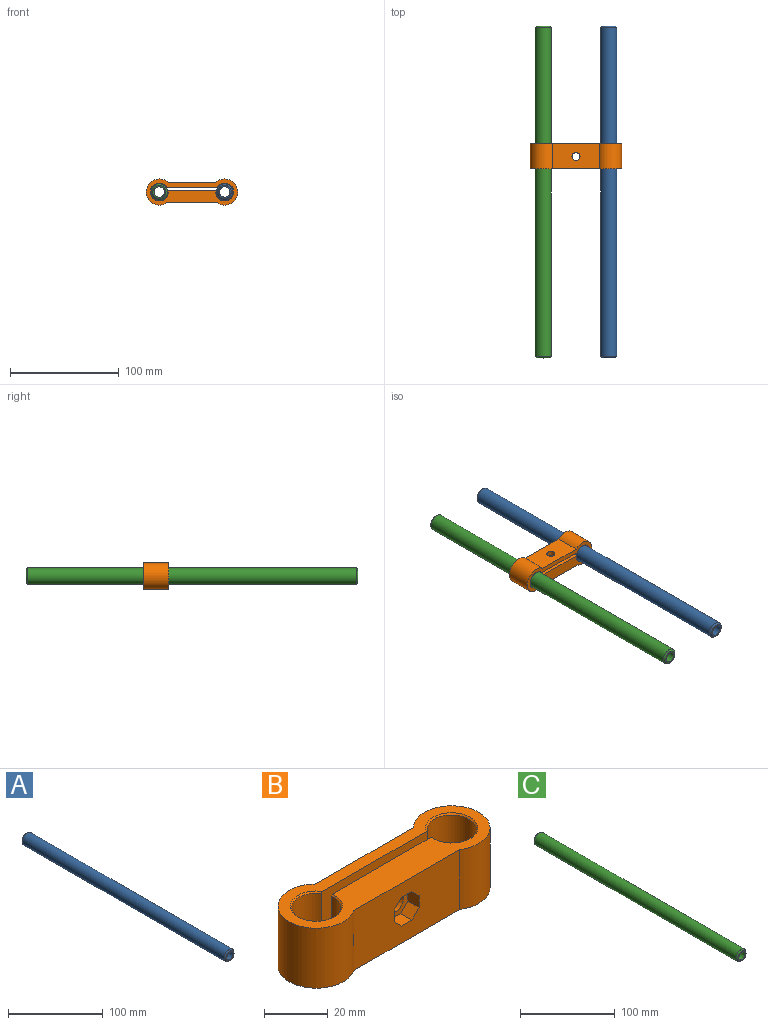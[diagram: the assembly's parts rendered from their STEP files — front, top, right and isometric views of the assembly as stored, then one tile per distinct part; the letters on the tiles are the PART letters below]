
ASSEMBLY  parts=3 mates=3
PART A: 6 faces, bbox 15x304.8x15 mm
  f0: cylinder r=4.8mm len=304.8mm, axis (0,1,0), area 9192.6mm2, adj f2,f3
  f1: cylinder r=7.5mm len=301.8mm, axis (0,1,0), area 14222mm2, adj f4,f5
  f2: plane 12x12mm, normal (0,-1,0), area 40.7mm2, adj f0,f5
  f3: plane 12x12mm, normal (0,1,0), area 40.7mm2, adj f0,f4
  f4: cone r=7.5mm half-angle=45deg, axis (0,-1,0), area 90mm2, adj f1,f3
  f5: cone r=6mm half-angle=45deg, axis (0,1,0), area 90mm2, adj f1,f2
PART B: 25 faces, bbox 84x24x23 mm
  f0: plane 46.87x23mm, normal (0,-1,0), area 977.8mm2, adj f1,f3,f8,f9,f16,f17,f18,f19
  f1: cylinder r=12mm len=24mm, axis (0,0,1), area 1238.6mm2, adj f0,f2,f8,f9
  f2: plane 43.34x23mm, normal (0,1,0), area 954.5mm2, adj f1,f3,f8,f9,f11
  f3: cylinder r=12mm len=24mm, axis (0,0,1), area 1238.6mm2, adj f0,f2,f8,f9
  f4: plane 44.73x23mm, normal (0,1,0), area 985.9mm2, adj f5,f7,f8,f9,f10,f12,f13,f14
  f5: cylinder r=7.7mm len=22mm, axis (0,0,1), area 987.2mm2, adj f4,f6,f12,f15
  f6: plane 47.18x23.01mm, normal (0,-1,0), area 1041.9mm2, adj f5,f7,f8,f9,f11,f12,f13,f14
  f7: cylinder r=7.7mm len=22mm, axis (0,0,1), area 987.2mm2, adj f4,f6,f13,f14
  f8: plane 84x24mm, normal (0,0,-1), area 1061.5mm2, adj f0,f1,f2,f3,f4,f6,f12,f13
  f9: plane 84x24mm, normal (0,0,1), area 1061.5mm2, adj f0,f1,f2,f3,f4,f6,f14,f15
  f10: cylinder r=3.67mm len=7.35mm, axis (0,1,0), area 139.6mm2, adj f4,f24
  f11: cylinder r=3.67mm len=7.35mm, axis (0,1,0), area 101.1mm2, adj f2,f6
  f12: cone r=8.2mm half-angle=45deg, axis (0,0,-1), area 32.9mm2, adj f4,f5,f6,f8
  f13: cone r=7.7mm half-angle=45deg, axis (0,0,-1), area 32.9mm2, adj f4,f6,f7,f8
  f14: cone r=8.2mm half-angle=45deg, axis (0,0,1), area 32.9mm2, adj f4,f6,f7,f9
  f15: cone r=7.7mm half-angle=45deg, axis (0,0,1), area 32.9mm2, adj f4,f5,f6,f9
  f16: plane 5x3.22mm, normal (0.71,0,-0.71), area 22.8mm2, adj f0,f17,f23,f24
  f17: plane 5x4.56mm, normal (1,0,0), area 22.8mm2, adj f0,f16,f18,f24
  f18: plane 5x3.22mm, normal (0.71,0,0.71), area 22.8mm2, adj f0,f17,f19,f24
  f19: plane 5x4.56mm, normal (0,0,1), area 22.8mm2, adj f0,f18,f20,f24
  f20: plane 5x3.22mm, normal (-0.71,0,0.71), area 22.8mm2, adj f0,f19,f21,f24
  f21: plane 5x4.56mm, normal (-1,0,0), area 22.8mm2, adj f0,f20,f22,f24
  f22: plane 5x3.22mm, normal (-0.71,0,-0.71), area 22.8mm2, adj f0,f21,f23,f24
  f23: plane 5x4.56mm, normal (0,0,-1), area 22.8mm2, adj f0,f16,f22,f24
  f24: plane 11x11mm, normal (0,-1,0), area 57.8mm2, adj f10,f16,f17,f18,f19,f20,f21,f22
PART C: 6 faces, bbox 15x304.8x15 mm
  f0: cylinder r=4.8mm len=304.8mm, axis (0,1,0), area 9192.6mm2, adj f2,f3
  f1: cylinder r=7.5mm len=301.8mm, axis (0,1,0), area 14222mm2, adj f4,f5
  f2: plane 12x12mm, normal (0,-1,0), area 40.7mm2, adj f0,f5
  f3: plane 12x12mm, normal (0,1,0), area 40.7mm2, adj f0,f4
  f4: cone r=7.5mm half-angle=45deg, axis (0,-1,0), area 90mm2, adj f1,f3
  f5: cone r=6mm half-angle=45deg, axis (0,1,0), area 90mm2, adj f1,f2
PLACE A rot(axis=(1,0,0),180deg) t=(-45.59,-31.65,-0.84)mm
PLACE B rot(axis=(1,0,0),90deg) t=(-45.64,47.76,-5.84)mm
PLACE C t=(-45.69,-31.65,-0.84)mm
MATE parallel C.f1 <-> A.f1  axis (0,-1,0) through (-75.64,-184.05,-0.84)mm
MATE slider B.f3 <-> C.f1  axis (0,-1,0) through (-75.64,-9.65,-0.84)mm
MATE slider A.f1 <-> B.f1  axis (0,-1,0) through (-15.64,-31.65,-0.84)mm
